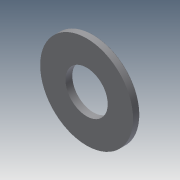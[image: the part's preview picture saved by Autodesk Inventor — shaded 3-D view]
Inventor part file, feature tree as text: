
AUTODESK INVENTOR PART (.ipt)
format: ipt  version: 2015 (Build 190159000, 159)  size: 89,088 bytes
history: native  units: mm
features: extrude x1, fillet x1, sketch x1
ambient origin geometry x8: Origin, YZ Plane, XZ Plane, XY Plane, X Axis, Y Axis, Z Axis, Center Point
bodies: Solid1 (feature_tree)
feature tree (3):
  extrude  "Extrusion1"  Depth=0.2mm
  fillet  "Fillet1"  Radius=1.6mm
  sketch  "Sketch1"  dims[d0=10.0mm d1=22.0mm d2=1.6mm d3=0.0mm d4=0.2mm]
